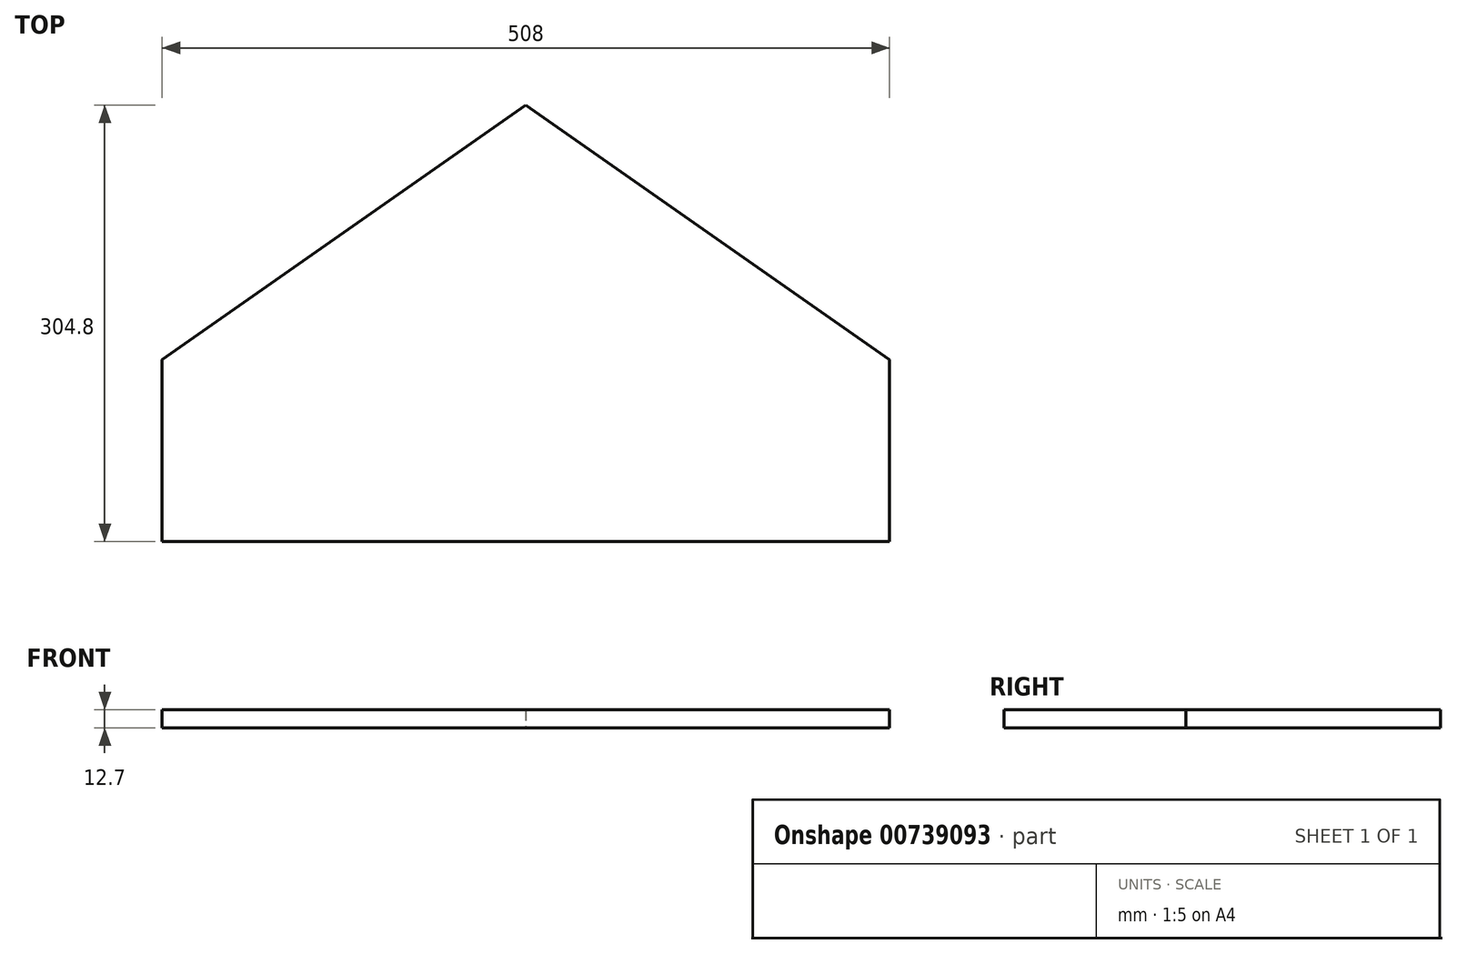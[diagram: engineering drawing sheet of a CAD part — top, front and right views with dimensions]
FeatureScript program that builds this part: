
annotation { "Feature Type Name" : "Feature", "Feature Type Description" : "" }
export const myFeature = defineFeature(function(context is Context, id is Id, definition is map)
    precondition{}
    {
        {
            var Q0;
            Q0=qCreatedBy(makeId("Top.planeOp"),FACE);
            var sketch = newSketch(context, id + "F0", { "sketchPlane" : qUnion([Q0])});
            skLineSegment(sketch, "E0", {"start": v(-254, 0) * mm, "end": v(254, 0) * mm});
            skLineSegment(sketch, "E1", {"start": v(254, 0) * mm, "end": v(254, 127) * mm});
            skLineSegment(sketch, "E2", {"start": v(254, 127) * mm, "end": v(0, 304.8) * mm});
            skLineSegment(sketch, "E3.MirrorCS", {"start": v(-254, 127) * mm, "end": v(0, 304.8) * mm});
            skLineSegment(sketch, "E4.MirrorCS", {"start": v(-254, 0) * mm, "end": v(-254, 127) * mm});
            skLineSegment(sketch, "E5", {"start": v(254, 127) * mm, "end": v(435.43, 0) * mm, "construction": true});
            skSolve(sketch);
        }
        {
            var Q0;
            Q0=makeQuery(id+"F0.imprint","IMPRINT",FACE,{"disambiguationData":[TD([[makeQuery(id+"F0.imprint","IMPRINT",EDGE,{"derivedFrom":sQuery(id+"F0.wireOp",EDGE,"E0")}),1.0]])]});
            extrude(context, id + "F1", {"entities" : qUnion([Q0]), "depth" : 12.7 * mm, "offsetDistance" : 25.4 * mm});
        }
    });
